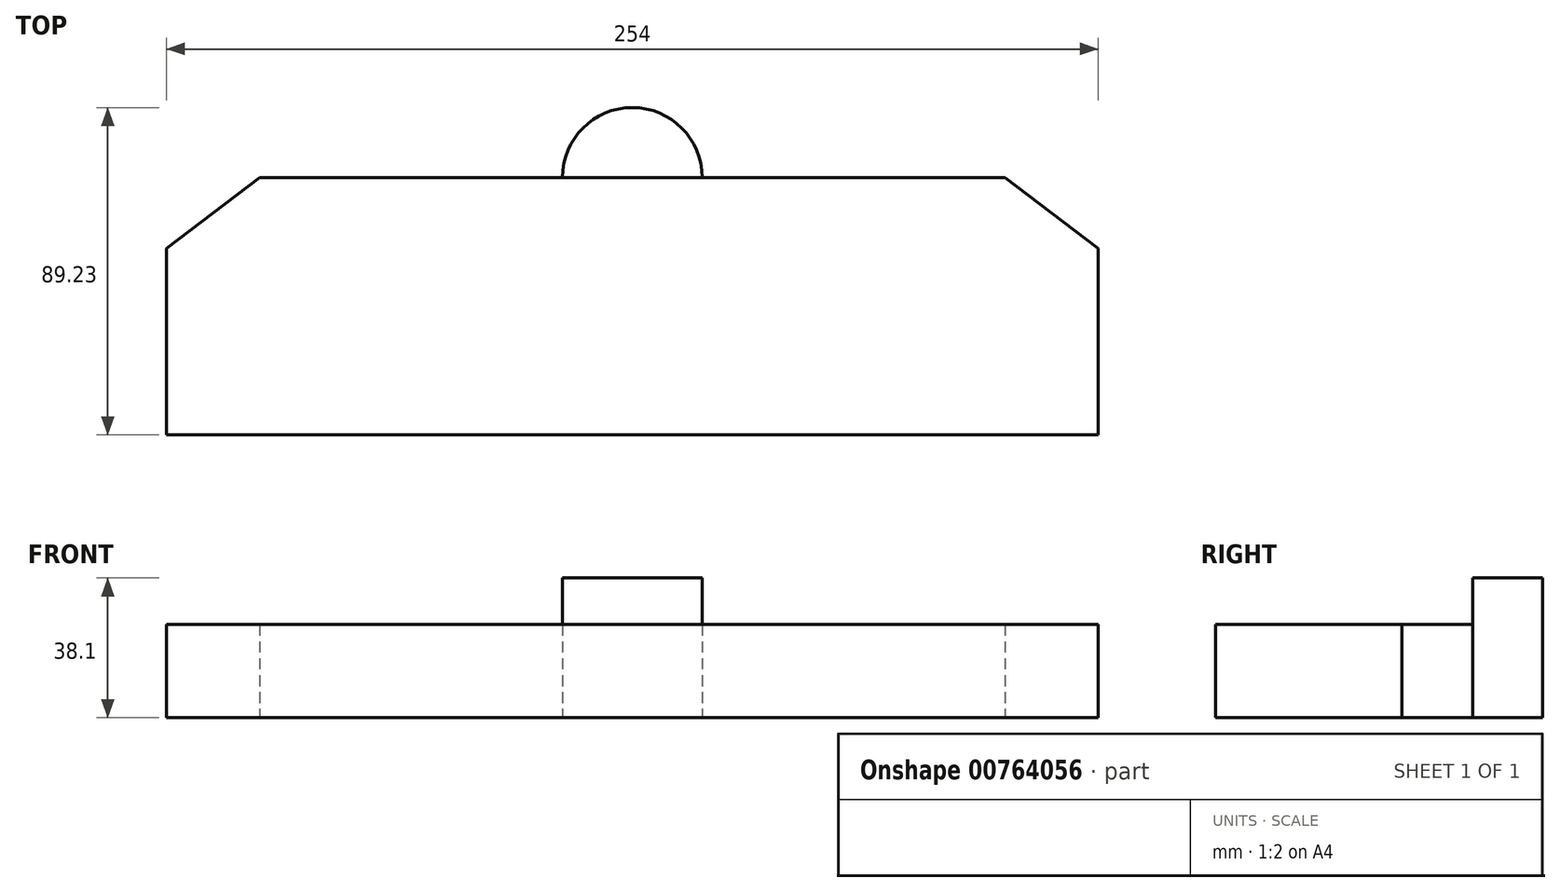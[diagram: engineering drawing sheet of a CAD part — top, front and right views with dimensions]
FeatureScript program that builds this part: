
annotation { "Feature Type Name" : "Feature", "Feature Type Description" : "" }
export const myFeature = defineFeature(function(context is Context, id is Id, definition is map)
    precondition{}
    {
        {
            var Q0;
            Q0=qCreatedBy(makeId("Top.planeOp"),FACE);
            var sketch = newSketch(context, id + "F0", { "sketchPlane" : qUnion([Q0])});
            skLineSegment(sketch, "E0", {"start": v(0, 50.8) * mm, "end": v(25.4, 70.18) * mm});
            skLineSegment(sketch, "E1", {"start": v(228.6, 70.18) * mm, "end": v(25.4, 70.18) * mm});
            skLineSegment(sketch, "E2", {"start": v(228.6, 70.18) * mm, "end": v(254, 50.8) * mm});
            skLineSegment(sketch, "E3", {"start": v(254, 50.8) * mm, "end": v(254, 0) * mm});
            skLineSegment(sketch, "E4", {"start": v(254, 0) * mm, "end": v(0, 0) * mm});
            skLineSegment(sketch, "E5", {"start": v(0, 0) * mm, "end": v(0, 50.8) * mm});
            skCircle(sketch, "E6", {"center": v(127, 70.18) * mm, "radius": 19.05 * mm});
            skSolve(sketch);
        }
        {
            var Q0;
            {var subQ0=sQuery(id+"F0.wireOp",EDGE,"E6");var subQ1=sQuery(id+"F0.wireOp",EDGE,"E1");var subQ2=makeQuery(id+"F0.imprint","INTERSECT",VERTEX,{"disambiguationData":[OD(0.0)],"derivedFrom":[subQ1,subQ0]});Q0=makeQuery(id+"F0.imprint","IMPRINT",FACE,{"disambiguationData":[TD([[makeQuery(id+"F0.imprint","IMPRINT",EDGE,{"disambiguationData":[TD([[subQ2,-1.0]])],"derivedFrom":subQ1}),-1.0]])]});}
            var Q1;
            {var subQ0=sQuery(id+"F0.wireOp",EDGE,"E6");var subQ1=sQuery(id+"F0.wireOp",EDGE,"E1");var subQ2=makeQuery(id+"F0.imprint","INTERSECT",VERTEX,{"disambiguationData":[OD(0.0)],"derivedFrom":[subQ1,subQ0]});Q1=makeQuery(id+"F0.imprint","IMPRINT",FACE,{"disambiguationData":[TD([[makeQuery(id+"F0.imprint","IMPRINT",EDGE,{"disambiguationData":[TD([[subQ2,-1.0]])],"derivedFrom":subQ1}),1.0]])]});}
            var Q2;
            {var subQ2=sQuery(id+"F0.wireOp",EDGE,"E0");Q2=makeQuery(id+"F0.imprint","IMPRINT",FACE,{"disambiguationData":[TD([[makeQuery(id+"F0.imprint","IMPRINT",EDGE,{"derivedFrom":subQ2}),-1.0]])]});}
            extrude(context, id + "F1", {"entities" : qUnion([Q0, Q1, Q2]), "depth" : 25.4 * mm, "offsetDistance" : 25.4 * mm});
        }
        {
            var Q0;
            {var subQ0=sQuery(id+"F0.wireOp",EDGE,"E6");var subQ1=sQuery(id+"F0.wireOp",EDGE,"E1");var subQ2=makeQuery(id+"F0.imprint","INTERSECT",VERTEX,{"disambiguationData":[OD(0.0)],"derivedFrom":[subQ1,subQ0]});Q0=makeQuery(id+"F0.imprint","IMPRINT",FACE,{"disambiguationData":[TD([[makeQuery(id+"F0.imprint","IMPRINT",EDGE,{"disambiguationData":[TD([[subQ2,-1.0]])],"derivedFrom":subQ1}),1.0]])]});}
            var sketch = newSketch(context, id + "F2", { "sketchPlane" : qUnion([Q0])});
            skSolve(sketch);
        }
        {
            var Q0;
            {var subQ0=sQuery(id+"F0.wireOp",EDGE,"E6");var subQ1=sQuery(id+"F0.wireOp",EDGE,"E1");var subQ2=makeQuery(id+"F0.imprint","INTERSECT",VERTEX,{"disambiguationData":[OD(0.0)],"derivedFrom":[subQ1,subQ0]});Q0=makeQuery(id+"F2.imprint","IMPRINT",FACE,{"disambiguationData":[TD([[makeQuery(id+"F2.imprint","IMPRINT",EDGE,{"derivedFrom":makeQuery(id+"F0.imprint","IMPRINT",EDGE,{"disambiguationData":[TD([[subQ2,-1.0]])],"derivedFrom":subQ1})}),1.0]])]});}
            var Q1;
            {var subQ0=sQuery(id+"F0.wireOp",EDGE,"E6");var subQ1=sQuery(id+"F0.wireOp",EDGE,"E1");var subQ2=makeQuery(id+"F0.imprint","INTERSECT",VERTEX,{"disambiguationData":[OD(0.0)],"derivedFrom":[subQ1,subQ0]});Q1=makeQuery(id+"F0.imprint","IMPRINT",FACE,{"disambiguationData":[TD([[makeQuery(id+"F0.imprint","IMPRINT",EDGE,{"disambiguationData":[TD([[subQ2,-1.0]])],"derivedFrom":subQ1}),-1.0]])]});}
            extrude(context, id + "F3", {"entities" : qUnion([Q0, Q1]), "operationType" : NewBodyOperationType.ADD, "depth" : 38.1 * mm, "offsetDistance" : 25.4 * mm});
        }
    });
